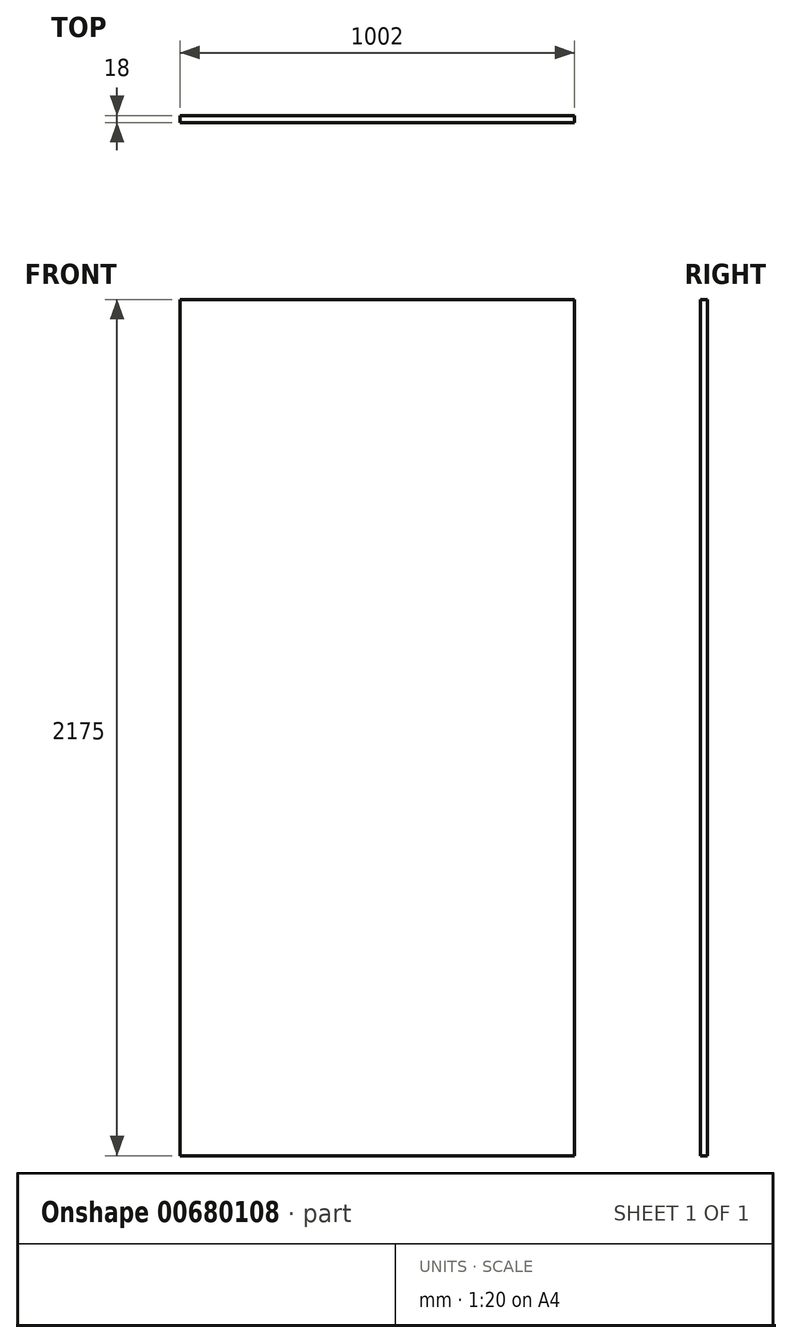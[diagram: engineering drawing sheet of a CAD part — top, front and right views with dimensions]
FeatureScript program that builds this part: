
annotation { "Feature Type Name" : "Feature", "Feature Type Description" : "" }
export const myFeature = defineFeature(function(context is Context, id is Id, definition is map)
    precondition{}
    {
        {
            var Q0;
            Q0=qCreatedBy(makeId("Front.planeOp"),FACE);
            var sketch = newSketch(context, id + "F0", { "sketchPlane" : qUnion([Q0])});
            skLineSegment(sketch, "E0.bottom", {"start": v(-501, 1087.5) * mm, "end": v(501, 1087.5) * mm});
            skLineSegment(sketch, "E0.top", {"start": v(-501, -1087.5) * mm, "end": v(501, -1087.5) * mm});
            skLineSegment(sketch, "E0.left", {"start": v(-501, 1087.5) * mm, "end": v(-501, -1087.5) * mm});
            skLineSegment(sketch, "E0.right", {"start": v(501, 1087.5) * mm, "end": v(501, -1087.5) * mm});
            skPoint(sketch, "E0.middle", {"position": v(0, 0) * mm});
            skSolve(sketch);
        }
        {
            var Q0;
            Q0=makeQuery(id+"F0.imprint","IMPRINT",FACE,{"disambiguationData":[TD([[makeQuery(id+"F0.imprint","IMPRINT",EDGE,{"derivedFrom":sQuery(id+"F0.wireOp",EDGE,"E0.bottom")}),-1.0]])]});
            extrude(context, id + "F1", {"entities" : qUnion([Q0]), "endBound" : BoundingType.SYMMETRIC, "depth" : 18 * mm, "offsetDistance" : 25 * mm});
        }
    });
